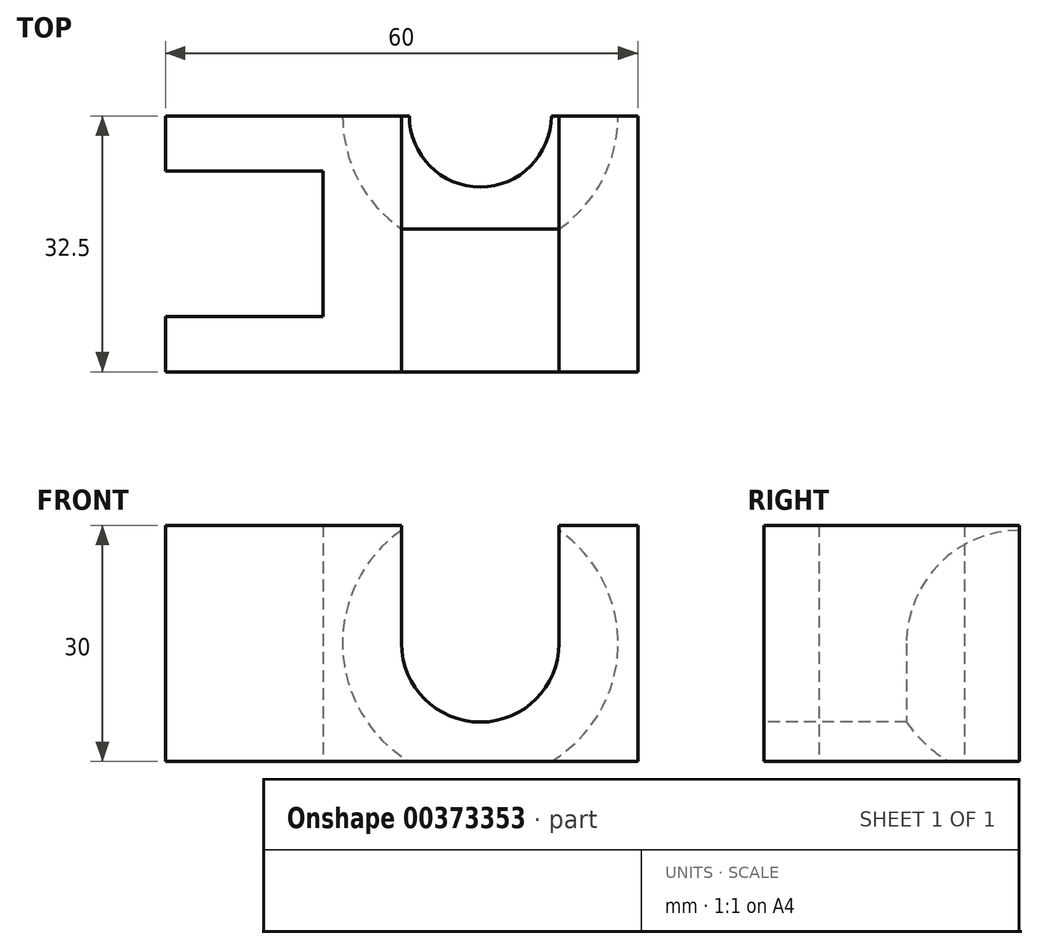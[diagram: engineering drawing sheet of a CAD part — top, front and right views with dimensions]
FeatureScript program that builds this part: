
annotation { "Feature Type Name" : "Feature", "Feature Type Description" : "" }
export const myFeature = defineFeature(function(context is Context, id is Id, definition is map)
    precondition{}
    {
        {
            var Q0;
            Q0=qCreatedBy(makeId("Top.planeOp"),FACE);
            var sketch = newSketch(context, id + "F0", { "sketchPlane" : qUnion([Q0])});
            skLineSegment(sketch, "E0", {"start": v(0, 0) * mm, "end": v(0, 7) * mm});
            skLineSegment(sketch, "E1", {"start": v(0, 7) * mm, "end": v(20, 7) * mm});
            skLineSegment(sketch, "E2", {"start": v(20, 7) * mm, "end": v(20, 25.5) * mm});
            skLineSegment(sketch, "E3", {"start": v(20, 25.5) * mm, "end": v(0, 25.5) * mm});
            skLineSegment(sketch, "E4", {"start": v(0, 25.5) * mm, "end": v(0, 32.5) * mm});
            skLineSegment(sketch, "E5", {"start": v(0, 32.5) * mm, "end": v(60, 32.5) * mm});
            skLineSegment(sketch, "E6", {"start": v(60, 32.5) * mm, "end": v(60, 0) * mm});
            skLineSegment(sketch, "E7", {"start": v(60, 0) * mm, "end": v(0, 0) * mm});
            skSolve(sketch);
        }
        {
            var Q0;
            Q0 = qSketchRegion(id + "F0", true);
            extrude(context, id + "F1", {"entities" : qUnion([Q0]), "depth" : 30 * mm});
        }
        {
            var Q0;
            Q0=makeQuery(id+"F1.opExtrude","SWEPT_FACE",FACE,{"disambiguationData":[OSD([sQuery(id+"F0.wireOp",EDGE,"E7")])]});
            var sketch = newSketch(context, id + "F2", { "sketchPlane" : qUnion([Q0])});
            skPoint(sketch, "E8", {"position": v(60, 15) * mm});
            skCircle(sketch, "E9", {"center": v(40, 15) * mm, "radius": 10 * mm});
            skLineSegment(sketch, "E10", {"start": v(30, 15) * mm, "end": v(30, 30) * mm});
            skLineSegment(sketch, "E11", {"start": v(50, 15) * mm, "end": v(50, 30) * mm});
            skLineSegment(sketch, "E12", {"start": v(50, 30) * mm, "end": v(30, 30) * mm});
            skPoint(sketch, "E13.0", {"position": v(20, 30) * mm});
            skPoint(sketch, "E14.0", {"position": v(60, 30) * mm});
            skLineSegment(sketch, "E15", {"start": v(20, 30) * mm, "end": v(60, 30) * mm, "construction": true});
            skPoint(sketch, "E16", {"position": v(40, 30) * mm});
            skSolve(sketch);
        }
        {
            var Q0;
            Q0 = qSketchRegion(id + "F2", true);
            extrude(context, id + "F3", {"entities" : qUnion([Q0]), "operationType" : NewBodyOperationType.REMOVE, "endBound" : BoundingType.THROUGH_ALL, "oppositeDirection" : true, "depth" : 25 * mm});
        }
        {
            var Q0;
            Q0=qCreatedBy(makeId("Top.planeOp"),FACE);
            var Q1;
            Q1=makeQuery(id+"F3.boolean.opBoolean","INTERSECT",VERTEX,{"derivedFrom":[makeQuery(id+"F1.opExtrude","SWEPT_FACE",FACE,{"disambiguationData":[OSD([sQuery(id+"F0.wireOp",EDGE,"E5")])]}),makeQuery(id+"F3.opExtrude","SWEPT_FACE",FACE,{"disambiguationData":[OSD([sQuery(id+"F2.wireOp",EDGE,"E9")])]}),makeQuery(id+"F3.opExtrude","SWEPT_FACE",FACE,{"disambiguationData":[OSD([sQuery(id+"F2.wireOp",EDGE,"E11")])]})]});
            cPlane(context, id + "F4", {"entities" : qUnion([Q0, Q1]), "cplaneType" : CPlaneType.PLANE_POINT, "offset" : 25 * mm, "width" : 150 * mm, "height" : 150 * mm});
        }
        {
            var Q0;
            Q0=qCreatedBy(id+"F4.planeOp",FACE);
            var sketch = newSketch(context, id + "F5", { "sketchPlane" : qUnion([Q0])});
            skPoint(sketch, "E17.0", {"position": v(40, 32.5) * mm});
            skArc(sketch, "E18", {"start": v(57.5, 32.5) * mm, "mid": v(52.37, 20.13) * mm, "end": v(40, 15) * mm});
            skLineSegment(sketch, "E19", {"start": v(40, 32.5) * mm, "end": v(57.5, 32.5) * mm});
            skLineSegment(sketch, "E20", {"start": v(40, 32.5) * mm, "end": v(40, 15) * mm});
            skSolve(sketch);
        }
        {
            var Q0;
            Q0 = qSketchRegion(id + "F5", true);
            var Q1;
            Q1=sQuery(id+"F5.wireOp",EDGE,"E20");
            revolve(context, id + "F6", {"operationType" : NewBodyOperationType.REMOVE, "entities" : qUnion([Q0]), "axis" : qUnion([Q1]), "revolveType" : RevolveType.FULL, "oppositeDirection" : true});
        }
    });
